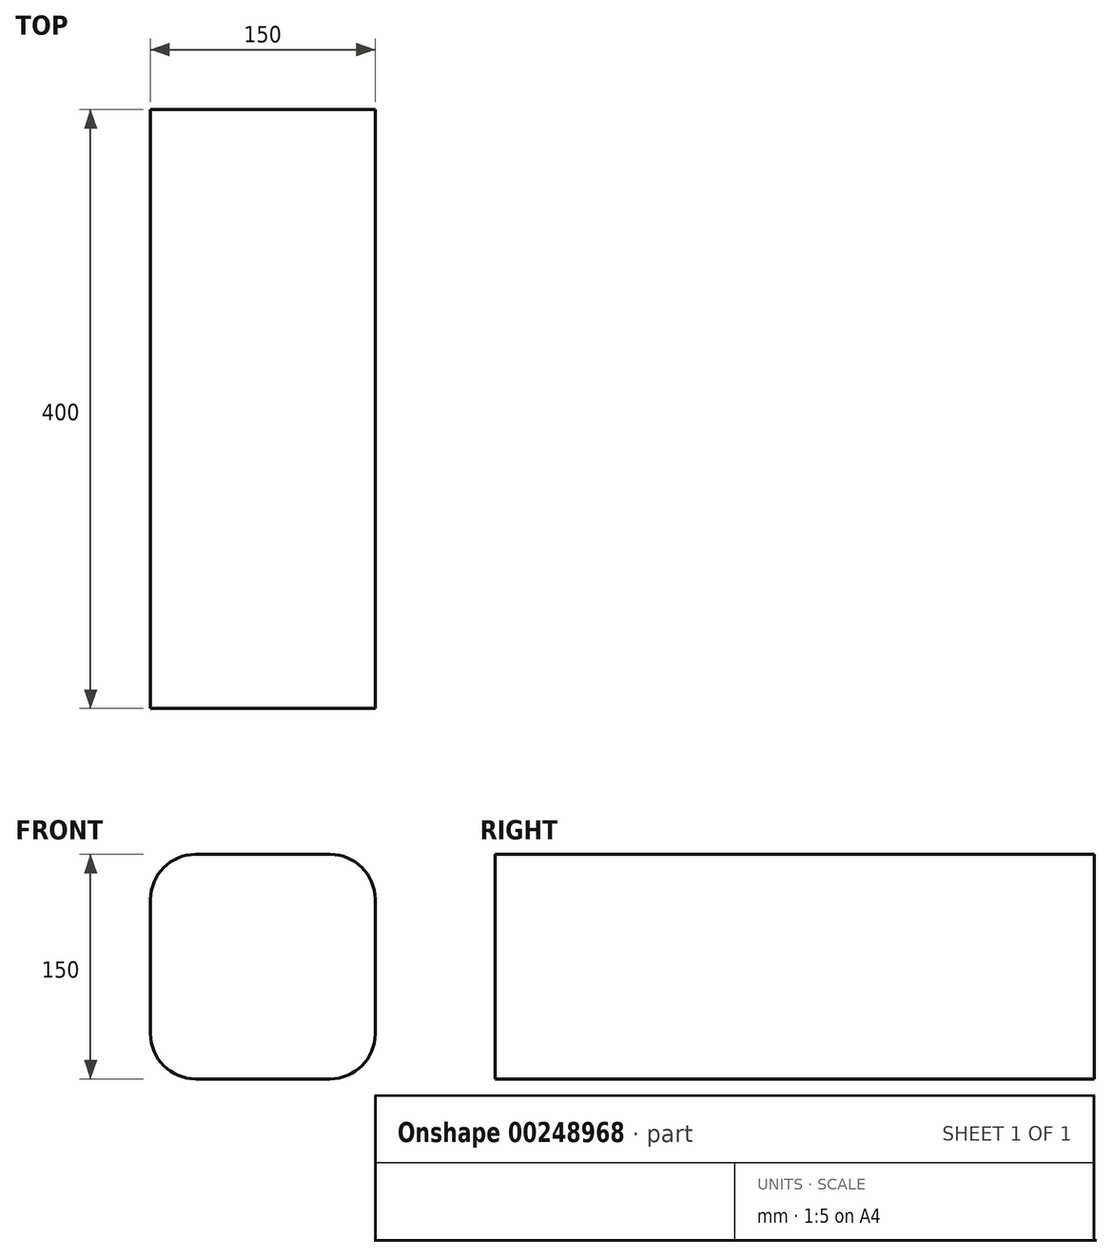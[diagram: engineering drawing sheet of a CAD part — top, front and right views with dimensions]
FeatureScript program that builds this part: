
annotation { "Feature Type Name" : "Feature", "Feature Type Description" : "" }
export const myFeature = defineFeature(function(context is Context, id is Id, definition is map)
    precondition{}
    {
        {
            var Q0;
            Q0=qCreatedBy(makeId("Front.planeOp"),FACE);
            var sketch = newSketch(context, id + "F0", { "sketchPlane" : qUnion([Q0])});
            skLineSegment(sketch, "E0.bottom", {"start": v(45, 75) * mm, "end": v(-45, 75) * mm});
            skLineSegment(sketch, "E0.top", {"start": v(45, -75) * mm, "end": v(-45, -75) * mm});
            skLineSegment(sketch, "E0.left", {"start": v(75, 45) * mm, "end": v(75, -45) * mm});
            skLineSegment(sketch, "E0.right", {"start": v(-75, 45) * mm, "end": v(-75, -45) * mm});
            skPoint(sketch, "E0.middle", {"position": v(0, 0) * mm});
            skPoint(sketch, "E1.visualSharp", {"position": v(75, 75) * mm});
            skArc(sketch, "E1.filletArc", {"start": v(75, 45) * mm, "mid": v(66.21, 66.21) * mm, "end": v(45, 75) * mm});
            skPoint(sketch, "E2.visualSharp", {"position": v(75, -75) * mm});
            skArc(sketch, "E2.filletArc", {"start": v(45, -75) * mm, "mid": v(66.21, -66.21) * mm, "end": v(75, -45) * mm});
            skPoint(sketch, "E3.visualSharp", {"position": v(-75, -75) * mm});
            skArc(sketch, "E3.filletArc", {"start": v(-75, -45) * mm, "mid": v(-66.21, -66.21) * mm, "end": v(-45, -75) * mm});
            skPoint(sketch, "E4.visualSharp", {"position": v(-75, 75) * mm});
            skArc(sketch, "E4.filletArc", {"start": v(-45, 75) * mm, "mid": v(-66.21, 66.21) * mm, "end": v(-75, 45) * mm});
            skSolve(sketch);
        }
        {
            var Q0;
            Q0 = qSketchRegion(id + "F0", true);
            extrude(context, id + "F1", {"entities" : qUnion([Q0]), "depth" : 400 * mm});
        }
    });
